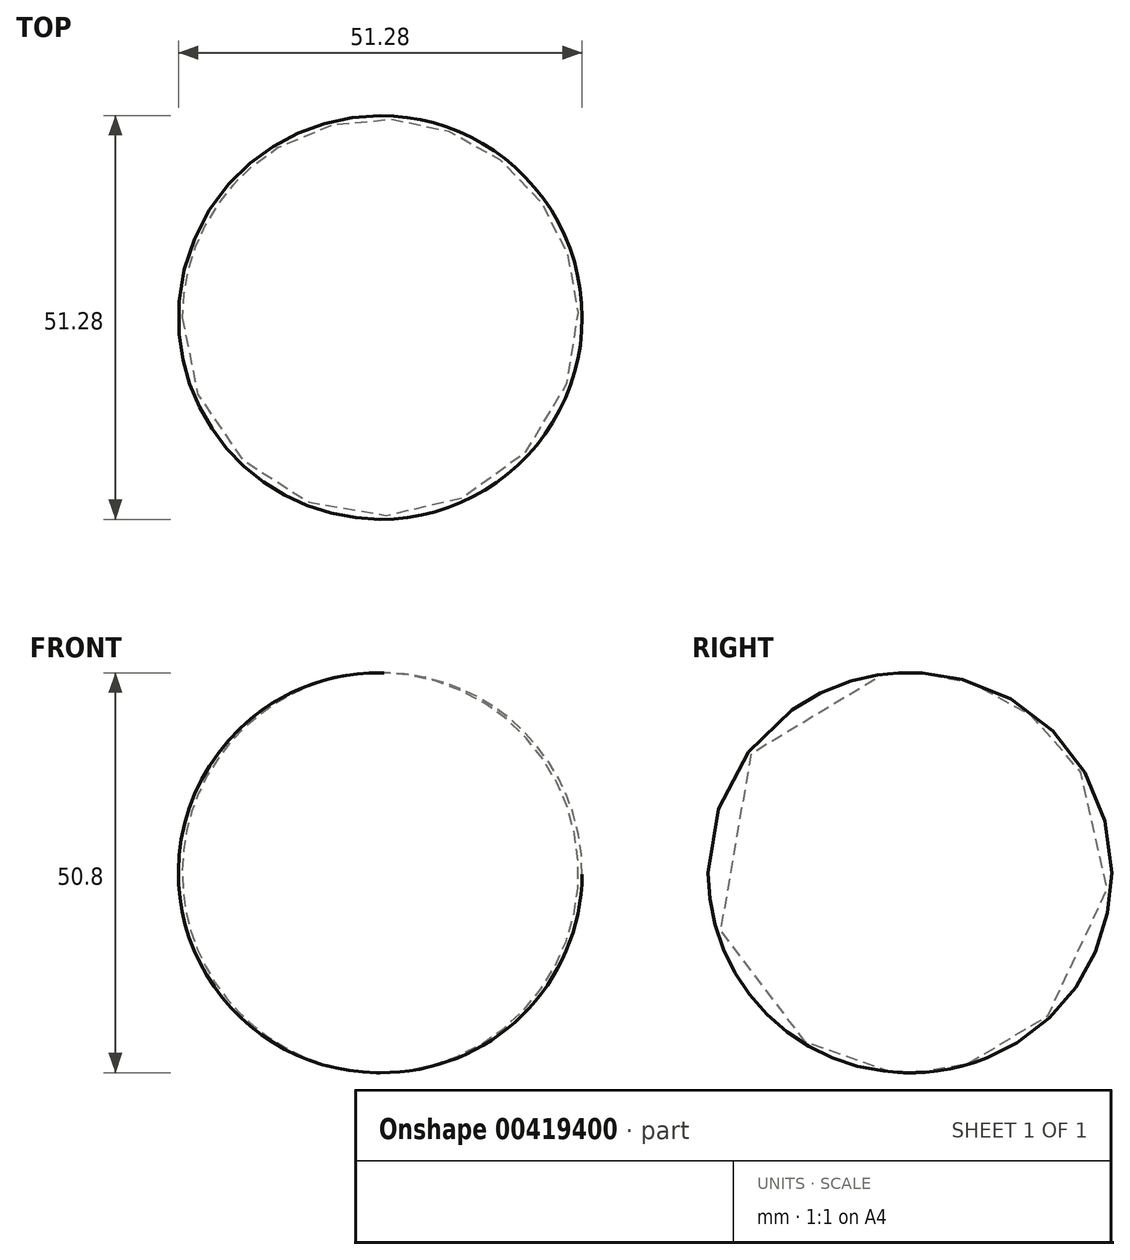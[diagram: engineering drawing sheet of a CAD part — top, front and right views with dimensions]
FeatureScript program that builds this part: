
annotation { "Feature Type Name" : "Feature", "Feature Type Description" : "" }
export const myFeature = defineFeature(function(context is Context, id is Id, definition is map)
    precondition{}
    {
        {
            var Q0;
            Q0=qCreatedBy(makeId("Front.planeOp"),FACE);
            var sketch = newSketch(context, id + "F0", { "sketchPlane" : qUnion([Q0])});
            skArc(sketch, "E0", {"start": v(0, 25.4) * mm, "mid": v(-25.4, 0.25) * mm, "end": v(-0.49, -25.4) * mm});
            skLineSegment(sketch, "E1", {"start": v(0, 25.4) * mm, "end": v(-0.49, -25.4) * mm});
            skSolve(sketch);
        }
        {
            var Q0;
            Q0 = qSketchRegion(id + "F0", true);
            var Q1;
            Q1=sQuery(id+"F0.wireOp",EDGE,"E1");
            revolve(context, id + "F1", {"entities" : qUnion([Q0]), "axis" : qUnion([Q1]), "revolveType" : RevolveType.FULL});
        }
    });
